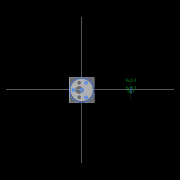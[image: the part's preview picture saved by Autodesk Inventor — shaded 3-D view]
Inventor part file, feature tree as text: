
AUTODESK INVENTOR PART (.ipt)
format: ipt  version: 2022.2 (Build 262287010, 287A)  size: 540,160 bytes
history: native  units: mm
features: other x20, extrude x20, sketch x18, pattern_circular x7, plane x6, fillet x2, move_body x2, revolve x2, draft x2, chamfer x2, loft x1
ambient origin geometry x8: Origin, YZ Plane, XZ Plane, XY Plane, X Axis, Y Axis, Z Axis, Center Point
bodies: Solid5 (feature_tree)
feature tree (82):
  other  "CrossSection1"
  sketch  "Sketch7"  dims[d90=15.767323mm]
  other  "Roller1"
  other  "Roller2"
  sketch  "Sketch22"  dims[d167=8.972256mm]
  sketch  "Sketch2"  dims[d57=4.025mm]
  sketch  "Sketch23"  dims[d173=10.814812mm]
  other  "RevRoller1"
  fillet  "Fillet1"  Radius=13.336791mm
  pattern_circular  "Circular Pattern13"  Count=360  [1 undecoded]
  move_body  "Move Body7"
  revolve  "Revolution13"  [1 undecoded]
  fillet  "Fillet3"  Radius=0.025mm
  pattern_circular  "Circular Pattern14"  [2 undecoded]
  move_body  "Move Body6"
  revolve  "Revolution14"  [1 undecoded]
  plane  "Work Plane7"
  sketch  "Sketch44"  dims[d349=17.374602mm]
  plane  "Work Plane8"
  loft  "Loft1"
  sketch  "Sketch46"  dims[d351=0.025mm]
  extrude  "Extrusion39"  TaperAngle=30.0deg  [1 undecoded]
  plane  "Work Plane9"
  sketch  "Sketch47"  dims[d352=0.025mm]
  extrude  "Extrusion40"  Depth=10.461905mm
  extrude  "Extrusion41"  Depth=10.461905mm
  extrude  "Extrusion42"  Depth=10.461905mm
  sketch  "Sketch48"  dims[d354=0.025mm]
  sketch  "Sketch49"  dims[d355=17.374329mm]
  extrude  "Extrusion43"  Depth=10.461905mm
  sketch  "Sketch51"  dims[d357=1.0mm]
  plane  "Work Plane10"
  sketch  "Sketch53"  dims[d358=90.0deg d359=0.5mm d360=60.0mm d361=360.0deg d363=30.0deg d367=8.1mm d369=4.014775mm d370=0.025mm d371=1.0mm d372=30.0deg d373=90.0deg d374=0.5mm d375=60.0mm d376=360.0deg d378=90.0deg d379=0.1mm d380=0.025mm d381=0.025mm d382=0.025mm d383=0.025mm d384=10.461905mm d385=0.0mm d386=0.0mm d391=1.0mm d392=53.5mm d393=1.5mm d394=1.5mm d395=1.5mm d396=1.5mm d397=90.0deg d398=90.0deg d399=90.0deg d400=53.5mm d401=10.461905mm d402=0.0mm d486=0.436332mm d487=0.5mm d488=2.0mm d489=0.0mm d490=20.0mm d495=2.5mm d496=8.0mm d506=13.856406mm d507=55.5mm d508=8.0mm d509=0.05mm d510=2.5mm d511=30.0deg d512=12.0mm d513=6.0mm d514=0.2mm d515=30.0deg d516=131.0mm d517=65.5mm d518=0.2mm d519=100.0mm d520=120.0mm d521=2.0mm d522=150.0mm d530=50.0mm d531=5.5mm d532=5.5mm d533=5.5mm d534=85.75mm d535=73.5mm d536=61.25mm d537=24.5mm d538=3.0mm d539=2.4mm d540=0.0mm d541=0.0mm d542=0.0mm d543=5.5mm d544=3.0mm d545=0.0mm d546=90.0mm d547=360.0deg d549=3.0mm d550=3.0mm d551=2.4mm d552=0.0mm d553=5.230953mm d554=0.0mm d555=2.4mm d556=0.0mm d557=5.230953mm d558=0.0mm d559=5.230953mm d560=0.0mm d561=90.0mm d562=360.0deg d564=60.0mm d565=360.0deg d567=5.5mm d568=5.5mm d569=3.0mm d570=0.0mm d571=5.230953mm d572=0.0mm d573=3.0mm d574=0.0mm d575=5.230953mm d576=0.0mm d577=90.0mm d578=360.0deg d580=60.0mm d581=360.0deg d584=20.0mm d585=8.0mm d587=1.75mm d589=3.0mm d592=2.0mm d593=12.0mm d594=12.0mm d600=0.5mm d601=2.0mm d602=45.0deg d603=0.5mm d604=2.0mm d605=45.0deg d606=0.436332mm d607=0.5mm d608=0.0mm d609=20.0mm d611=360.0deg d613=0.0mm d614=0.0mm d615=20.0mm d616=3.611mm d617=0.0mm d618=90.0deg d619=0.0mm d620=90.0deg d621=2.5mm d622=7.0mm d623=0.0mm d624=0.0mm d625=50.0mm d626=5.5mm d627=3.0mm d628=5.5mm d629=43.459mm d630=0.0mm d631=52.538mm d632=0.0mm d633=4.8mm d634=0.0mm d635=3.0mm d636=3.0mm d637=0.0mm d638=0.0mm d643=12.2mm d16=0.872665mm d17=0.872665mm d49=0.872665mm d50=0.872665mm d51=0.872665mm d52=0.872665mm d236=0.5mm d237=0.872665mm d238=0.5mm d239=0.872665mm d282=1.0mm d283=1.0mm d284=1.0mm d285=0.15mm d286=0.25mm d287=0.375mm d288=14.3117mm d289=0.75mm d290=20.594885mm d291=0.0625mm d292=0.75mm d293=0.375mm d405=0.5mm d406=0.872665mm d407=0.5mm d408=0.872665mm d413=0.5mm d414=0.872665mm d415=0.5mm d416=0.872665mm d417=0.5mm d418=0.872665mm d419=0.5mm d420=0.872665mm d421=0.872665mm d431=0.5mm d432=0.872665mm d433=0.5mm d434=0.872665mm d471=0.5mm d472=0.872665mm d473=0.5mm d474=0.872665mm d497=0.5mm d498=0.872665mm d499=0.5mm d500=0.872665mm d590=0.5mm d591=0.872665mm]
  other  "OuterRim_Top2"
  other  "OuterRim_Bottom2"
  extrude  "Rotor_Ring"  TaperAngle=30.0deg  [1 undecoded]
  draft  "FaceDraft2"
  sketch  "Sketch30"  dims[d201=53.5mm d232=0.0mm d233=3600.0mm]
  plane  "Work Plane5"
  other  "Rotor Featurs"
  other  "RotorRim_Bottom"
  extrude  "Extrusion24"  TaperAngle=90.0deg  [1 undecoded]
  extrude  "Extrusion25"  Depth=10.461905mm
  extrude  "Extrusion26"  Depth=10.461905mm
  pattern_circular  "Circular Pattern23"  Angle=360.0deg  [1 undecoded]
  sketch  "Sketch41"  dims[d346=0.025mm]
  extrude  "Extrusion27"  TaperAngle=90.0deg  [1 undecoded]
  extrude  "Extrusion28"  Depth=0.1mm
  pattern_circular  "Circular Pattern24"  [2 undecoded]
  extrude  "Extrusion29"  Depth=10.461905mm
  extrude  "Extrusion30"  Depth=10.461905mm
  extrude  "Extrusion31"  Depth=10.461905mm
  pattern_circular  "Circular Pattern25"  [2 undecoded]
  sketch  "Sketch42"  dims[d347=0.1mm]
  extrude  "Extrusion32"  TaperAngle=0.0deg  [1 undecoded]
  extrude  "Extrusion33"  TaperAngle=0.0deg  [1 undecoded]
  extrude  "Extrusion34"  Depth=10.461905mm
  extrude  "Extrusion35"  Depth=10.461905mm
  pattern_circular  "Circular Pattern26"  [2 undecoded]
  pattern_circular  "Circular Pattern27"  [2 undecoded]
  chamfer  "Chamfer1"  Distance=1.5mm
  chamfer  "Chamfer2"  Distance=1.5mm
  draft  "FaceDraft4"
  plane  "Work Plane6"
  sketch  "Sketch43"  dims[d348=0.1mm]
  extrude  "Extrusion37"  TaperAngle=90.0deg  [1 undecoded]
  extrude  "Extrusion38"  TaperAngle=90.0deg  [1 undecoded]
  other  "2D Equation Curve1"
  sketch  "Sketch40"  dims[d343=17.374329mm d344=17.374602mm d345=0.025mm]
  other  "Work Axis6"
  other  "Work Axis7"
  other  "Work Axis8"
  other  "Work Axis9"
  other  "Work Axis10"
  other  "Work Point1"
  other  "Work Point2"
  other  "Work Point3"
  other  "Work Point4"
  other  "Work Point5"
  sketch  "Sketch45"  dims[d350=17.374329mm]
  other  "Edges1"
  sketch  "Sketch50"  dims[d356=17.374602mm]
note: 22 required parameter values undecoded (feature->parameter linkage not recoverable at this tier; creation-order binding heuristic only, values carry confidence <= 0.55)